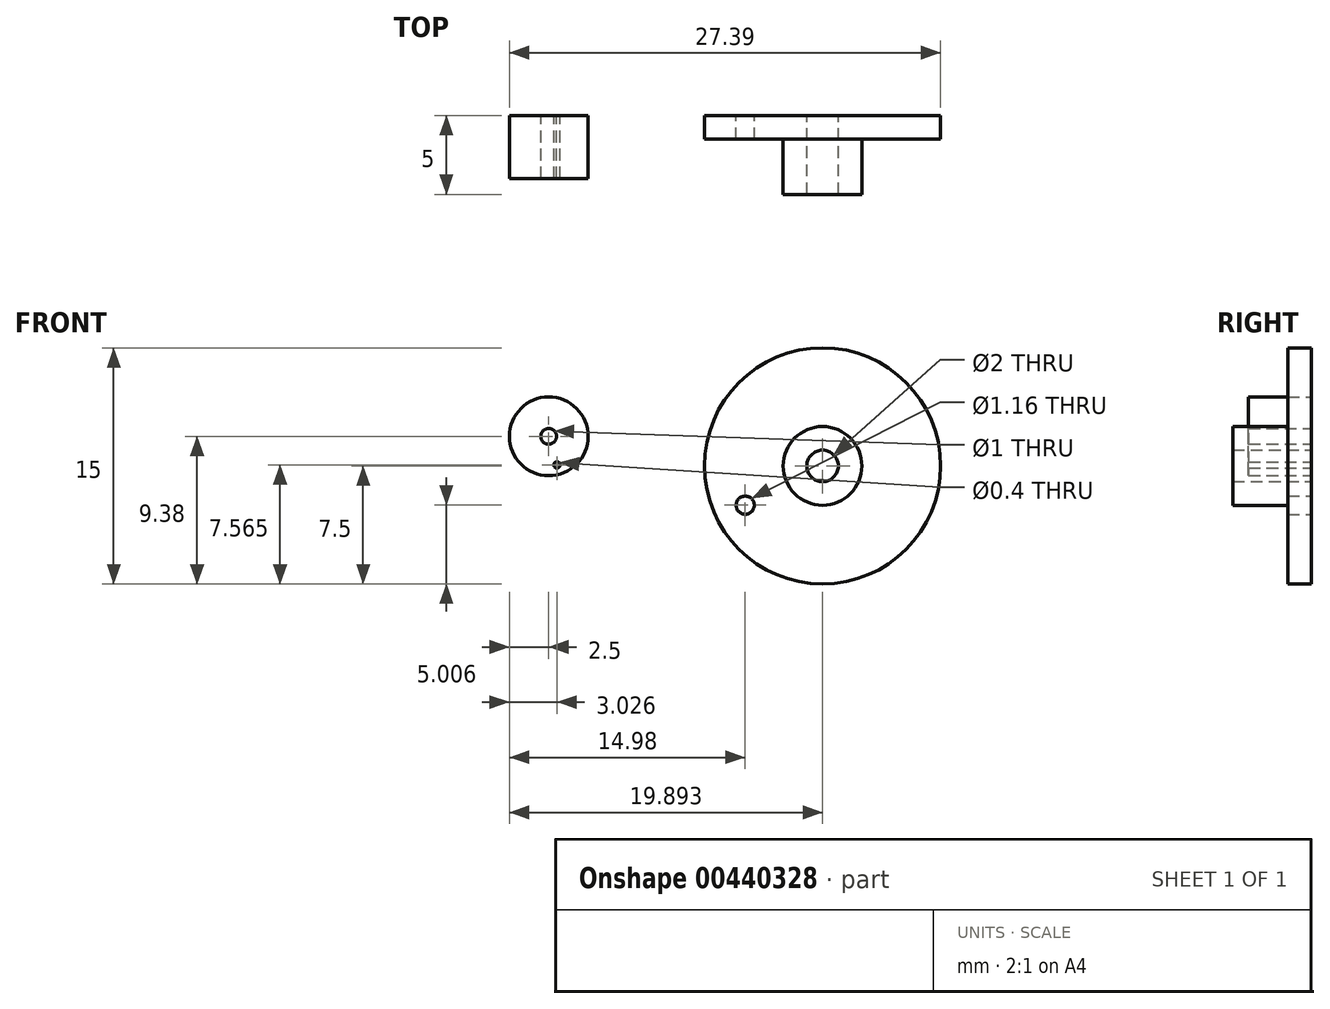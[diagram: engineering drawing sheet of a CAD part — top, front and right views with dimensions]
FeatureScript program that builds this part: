
annotation { "Feature Type Name" : "Feature", "Feature Type Description" : "" }
export const myFeature = defineFeature(function(context is Context, id is Id, definition is map)
    precondition{}
    {
        {
            var Q0;
            Q0=qCreatedBy(makeId("Front.planeOp"),FACE);
            var sketch = newSketch(context, id + "F0", { "sketchPlane" : qUnion([Q0])});
            skCircle(sketch, "E0", {"center": v(0, 0) * mm, "radius": 2.5 * mm});
            skCircle(sketch, "E1", {"center": v(0, 0) * mm, "radius": 0.5 * mm});
            skSolve(sketch);
        }
        {
            var Q0;
            Q0=makeQuery(id+"F0.imprint","IMPRINT",FACE,{"disambiguationData":[TD([[makeQuery(id+"F0.imprint","IMPRINT",EDGE,{"derivedFrom":sQuery(id+"F0.wireOp",EDGE,"E0")}),1.0]])]});
            extrude(context, id + "F1", {"entities" : qUnion([Q0]), "depth" : 4 * mm});
        }
        {
            var Q0;
            Q0=qCreatedBy(makeId("Front.planeOp"),FACE);
            var sketch = newSketch(context, id + "F2", { "sketchPlane" : qUnion([Q0])});
            skCircle(sketch, "E2", {"center": v(17.4, -1.88) * mm, "radius": 7.5 * mm});
            skCircle(sketch, "E3", {"center": v(17.4, -1.88) * mm, "radius": 1 * mm});
            skCircle(sketch, "E4", {"center": v(12.48, -4.37) * mm, "radius": 0.58 * mm});
            skSolve(sketch);
        }
        {
            var Q0;
            Q0=makeQuery(id+"F2.imprint","IMPRINT",FACE,{"disambiguationData":[TD([[makeQuery(id+"F2.imprint","IMPRINT",EDGE,{"derivedFrom":sQuery(id+"F2.wireOp",EDGE,"E2")}),1.0]])]});
            extrude(context, id + "F3", {"entities" : qUnion([Q0]), "depth" : 1.5 * mm});
        }
        {
            var Q0;
            Q0=makeQuery(id+"F3.opExtrude","CAP_FACE",FACE,{"disambiguationData":[OSD([sQuery(id+"F2.wireOp",EDGE,"E2"),sQuery(id+"F2.wireOp",EDGE,"E3")])],"isStart":false});
            var sketch = newSketch(context, id + "F4", { "sketchPlane" : qUnion([Q0])});
            skCircle(sketch, "E5", {"center": v(17.4, -1.88) * mm, "radius": 2.5 * mm});
            skSolve(sketch);
        }
        {
            var Q0;
            Q0=makeQuery(id+"F4.imprint","IMPRINT",FACE,{"disambiguationData":[TD([[makeQuery(id+"F4.imprint","IMPRINT",EDGE,{"derivedFrom":sQuery(id+"F4.wireOp",EDGE,"E5")}),1.0]])]});
            extrude(context, id + "F5", {"entities" : qUnion([Q0]), "operationType" : NewBodyOperationType.ADD, "depth" : 3.5 * mm});
        }
        {
            var Q0;
            Q0=makeQuery(id+"F1.opExtrude","CAP_FACE",FACE,{"disambiguationData":[OSD([sQuery(id+"F0.wireOp",EDGE,"E0"),sQuery(id+"F0.wireOp",EDGE,"E1")])],"isStart":true});
            var sketch = newSketch(context, id + "F6", { "sketchPlane" : qUnion([Q0])});
            skCircle(sketch, "E6", {"center": v(-0.53, -1.82) * mm, "radius": 0.2 * mm});
            skSolve(sketch);
        }
        {
            var Q0;
            Q0=makeQuery(id+"F6.imprint","IMPRINT",FACE,{"disambiguationData":[TD([[makeQuery(id+"F6.imprint","IMPRINT",EDGE,{"derivedFrom":sQuery(id+"F6.wireOp",EDGE,"E6")}),1.0]])]});
            extrude(context, id + "F7", {"entities" : qUnion([Q0]), "operationType" : NewBodyOperationType.REMOVE, "endBound" : BoundingType.THROUGH_ALL, "oppositeDirection" : true, "depth" : 2 * mm});
        }
    });
